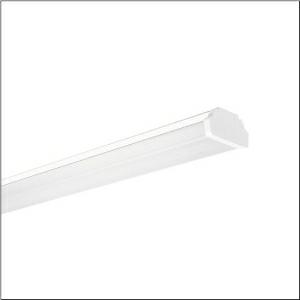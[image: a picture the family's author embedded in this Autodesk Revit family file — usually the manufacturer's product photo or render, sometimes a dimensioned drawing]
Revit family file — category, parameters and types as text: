
# Revit family: dus_r__31_gen_2_53bd812cv675c2_cf82
name_source: partatom
category: Lighting Fixtures
units: mm (PartAtom-declared; Revit-internal decimal feet)

## family parameters
Cut with Voids When Loaded = No
Host = Face
Light Source = No
Part Type = Normal
Room Calculation Point = No
Round Connector Dimension = Use Diameter
Shared = No

## types (1)
- --- (1 x LED, 7670 lm, 42.1 W, 6500K)
    Apparent Load = 42 VA
    CIE Flux Codes = 47 80 95 93 100
    Color Rendering = 80
    Color Temperature = 6500K
    Default Elevation = 1800 mm
    Description = DUS® 31 Gen.2, luminaire insert, of sheet steel, coil coated, white, length: 1.535mm, width: 81mm, height: 90mm, 5x system unit, system units: 307mm, LED rated luminous flux: 7.670lm, light colour: 865, control gear: ON/OFF Multilumen, CLOi, with plug, 3-pole, with phase selection, mains connection: 220..240V, AC, 50/60Hz, start of lifetime: 42W, end of service life: 50W, through-wiring accessed according to module size, primary optical cover: cover, of PMMA, light emission: direct distribution, primary light characteristic: symmetric, protection rating (complete): IP20, protection rating (LED compartment): IP50, insulation class (complete): insulation class I (protective earthing), certification: CE, ENEC, VDE, UKCA, impact resistance: IK03, permissible ambient temperature for indoor applications: -35..+50°C, corresponds to IFS (International Featured Standards) requirements for safety and quality in the food industry, reducing of maximum allowable ambient temperature of 5°C with ceiling mounting, packaging unit: 1 piece
    Height = 95 mm
    Lamp = 1 x LED
    Lamp Light Flux = 7670 lm
    Lamp Power = 42.1 W
    Lamp count = 1
    Length = 1535 mm
    Luminous efficacy = 182 lm/W
    Manufacturer = Siteco
    ModVariant = No
    Model = 53BD812CV675C2
    Mounting Place = Ceiling
    Mounting Type = Pendant
    Number of Poles = 1
    OnlyDefault = Yes
    Power Factor = 1
    Product Name = DUS® 31 Gen.2
    Product group = luminaire insert | ceiling pendant
    ProductGroupID = 902
    Protection Class = Protection class I
    Protection Degree = IP 20
    RLX_Detail_Level = 1
    RLX_Emergency_Light_Flux = 0 lm
    RLX_Emergency_Type = 0
    RLX_Emergency_Type_DB = No
    RlxData = <blob elided: 29773 chars, md5=6d3cbd59>
    Socket = socket
    Standby Power = 0 W
    System Light Flux = 7670 lm
    System Power = 42 W
    Type Comments = factory setting: luminous flux: 100 % | (A | C | E) | 98 mA
    Type Image = l_1319596.jpg
    URL = http://relux.com
    VarID = @adj_054201
    Voltage = 0 V
    Weight = 0.00 kg
    Width = 81 mm

## geometry (parser evidence)
native form markers: Blend x4, Sweep x14
no freeform markers — native parametric forms only
